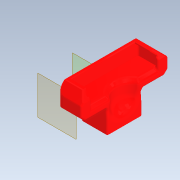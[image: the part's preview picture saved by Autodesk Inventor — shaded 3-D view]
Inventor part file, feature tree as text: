
AUTODESK INVENTOR PART (.ipt)
format: ipt  version: 2022.1 (Build 261234020, 234B)  size: 1,689,088 bytes
history: native  units: mm
features: fillet x21, delete_face x15, sketch x14, projected_geometry x14, extrude x13, other x7, direct_edit x5, chamfer x5, plane x3, reference x2, move_body x2, hole x1
ambient origin geometry x8: Origin, YZ Plane, XZ Plane, XY Plane, X Axis, Y Axis, Z Axis, Center Point
bodies: Volumenkörper1 (feature_tree), Body1 (feature_tree)
feature tree (102):
  extrude  "Extrusion1"  Depth=10.0mm
  extrude  "Extrusion4"  Depth=2.0mm TaperAngle=45.0deg
  direct_edit  "Direktbearbeitung2"
  direct_edit  "Direktbearbeitung3"
  direct_edit  "Direktbearbeitung4"
  chamfer  "Fase1"  Distance=2.0mm
  fillet  "Rundung7"  Radius=18.0mm
  fillet  "Rundung8"  Radius=25.0mm
  fillet  "Rundung9"  Radius=25.0mm
  fillet  "Rundung10"  Radius=1.0mm
  delete_face  "Fläche löschen1"
  extrude  "Extrusion5"  Depth=1.0mm
  extrude  "Extrusion6"  Depth=10.0mm
  fillet  "Rundung11"  Radius=17.0mm
  delete_face  "Fläche löschen2"
  extrude  "Extrusion7"  Depth=2.0mm
  chamfer  "Fase2"  [1 undecoded]
  fillet  "Rundung12"  Radius=0.4mm
  fillet  "Rundung13"  Radius=16.0mm
  fillet  "Rundung14"  Radius=5.0mm
  delete_face  "Fläche löschen3"
  delete_face  "Fläche löschen4"
  direct_edit  "Direktbearbeitung5"
  delete_face  "Fläche löschen5"
  delete_face  "Fläche löschen6"
  hole  "Bohrung1"  [1 undecoded]
  fillet  "Rundung15"  Radius=4.0mm
  chamfer  "Fase3"  Distance=1.0mm
  extrude  "Extrusion8"  Depth=1.0mm
  chamfer  "Fase5"  Angle=45.0deg  [1 undecoded]
  extrude  "Extrusion9"  Depth=1.0mm
  fillet  "Rundung16"  [1 undecoded]
  fillet  "Rundung17"  [1 undecoded]
  fillet  "Rundung18"  Radius=1.0mm
  fillet  "Rundung19"  Radius=1.0mm
  delete_face  "Fläche löschen7"
  plane  "Arbeitsebene1"
  extrude  "Extrusion10"  Depth=1.0mm
  plane  "Arbeitsebene3"
  extrude  "Extrusion11"  Depth=2.0mm TaperAngle=45.0deg
  fillet  "Rundung20"  Radius=9.0mm
  delete_face  "Fläche löschen8"
  delete_face  "Fläche löschen9"
  delete_face  "Fläche löschen10"
  fillet  "Rundung21"  [1 undecoded]
  fillet  "Rundung22"  Radius=0.552mm
  chamfer  "Fase7"  Distance=0.3mm
  direct_edit  "Direktbearbeitung8"
  extrude  "Extrusion12"  Depth=1.0mm
  delete_face  "Fläche löschen11"
  fillet  "Rundung23"  Radius=0.4mm
  delete_face  "Fläche löschen12"
  delete_face  "Fläche löschen13"
  fillet  "Rundung24"  Radius=1.0mm
  fillet  "Rundung25"  [1 undecoded]
  delete_face  "Fläche löschen14"
  fillet  "Rundung26"  [1 undecoded]
  fillet  "Rundung27"  Radius=30.0mm
  extrude  "Extrusion13"  [1 undecoded]
  extrude  "Extrusion14"  [1 undecoded]
  delete_face  "Fläche löschen15"
  plane  "Arbeitsebene4"
  extrude  "Extrusion15"  [1 undecoded]
  sketch  "Skizze1"  dims[d0=10.0mm d1=0.0mm d17=1.75mm]
  projected_geometry  "Projizierte Kontur1"
  projected_geometry  "Projizierte Kontur2"
  projected_geometry  "Projizierte Kontur3"
  projected_geometry  "Projizierte Kontur4"
  sketch  "Skizze4"  dims[d18=0.0mm d19=0.0mm d20=1.75mm d21=2.0mm d22=45.0deg]
  projected_geometry  "Projizierte Kontur12"
  sketch  "Skizze5"  dims[d23=0.5mm]
  sketch  "Skizze6"  dims[d24=0.55mm]
  sketch  "Skizze7"  dims[d25=1.0mm]
  projected_geometry  "Projizierte Kontur13"
  sketch  "Skizze8"  dims[d26=1.0mm d27=2.0mm d28=0.0mm d29=18.0mm d30=25.0mm d31=25.0mm d32=1.0mm]
  sketch  "Skizze9"  dims[d33=0.0mm d34=0.0mm d35=1.0mm]
  projected_geometry  "Projizierte Kontur14"
  sketch  "Skizze10"  dims[d36=10.0mm d37=10.0mm d38=17.0mm d39=0.0mm]
  projected_geometry  "Projizierte Kontur15"
  sketch  "Skizze11"  dims[d40=2.0mm d41=2.0mm d42=45.0deg d43=2.0mm]
  projected_geometry  "Projizierte Kontur16"
  sketch  "Skizze12"  dims[d44=2.0mm]
  projected_geometry  "Projizierte Kontur17"
  sketch  "Skizze13"  dims[d45=1.0mm d46=0.0mm d47=0.0mm d48=-3.5mm]
  sketch  "Skizze14"  dims[d49=6.15mm d50=6.0mm d51=4.0mm d52=2.0mm d53=90.0deg d54=8.0mm d55=0.0mm d56=0.4mm]
  sketch  "Skizze15"  dims[d57=0.4mm d58=2.0mm d59=45.0deg d69=16.0mm d70=0.0mm]
  reference  "Referenz1"
  reference  "Referenz2"
  sketch  "Skizze16"  dims[d71=15.0mm d72=2.0mm d73=45.0deg d74=5.0mm d75=0.0mm d76=8.0mm d77=4.0mm d78=1.0mm d82=4.0mm d83=45.0deg d84=1.0mm d85=0.0mm d86=0.0mm d87=0.0mm d88=0.0mm d89=1.0mm d90=1.0mm d91=1.0mm d92=0.4mm d93=2.0mm d94=45.0deg d95=0.0mm d96=0.0mm d97=9.0mm d98=0.0mm d99=0.0mm d100=0.552mm d101=0.3mm d102=0.55mm d103=0.4mm d104=1.0mm d105=0.0mm d106=0.0mm d107=0.0mm d108=0.0mm d109=30.0mm d110=0.0mm]
  projected_geometry  "Projizierte Kontur18"
  projected_geometry  "Projizierte Kontur19"
  projected_geometry  "Projizierte Kontur20"
  projected_geometry  "Projizierte Kontur21"
  other  "Löschen4"
  other  "Löschen5"
  other  "Löschen6"
  other  "Löschen7"
  move_body  "Verschieben1"
  move_body  "Verschieben4"
  other  "<userpath>\Desktop\RAMA_SBNG\BedPan\BucketR.iam"
  other  "BucketR.iam"
  other  "Bucket_Rama:1"
note: 11 required parameter values undecoded (feature->parameter linkage not recoverable at this tier; creation-order binding heuristic only, values carry confidence <= 0.55)
